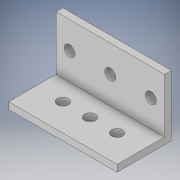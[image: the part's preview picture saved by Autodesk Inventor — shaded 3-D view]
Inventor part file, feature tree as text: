
AUTODESK INVENTOR PART (.ipt)
format: ipt  version: 2018 (Build 220112000, 112)  size: 133,120 bytes
history: native  units: in
note: dims shown in document units (in); Inventor stores cm internally (conversion verified against a paired STEP export)
features: extrude x3, sketch x3
ambient origin geometry x8: Origin, YZ Plane, XZ Plane, XY Plane, X Axis, Y Axis, Z Axis, Center Point
bodies: Solid1 (feature_tree)
feature tree (6):
  extrude  "Extrusion1"  Depth=1.0in
  extrude  "Extrusion2"  Depth=0.125in
  extrude  "Extrusion3"  Depth=2.0in
  sketch  "Sketch1"  dims[d0=0.125in d1=1.0in]
  sketch  "Sketch2"  dims[d2=1.0in d3=0.125in]
  sketch  "Sketch3"  dims[d4=2.0in d5=0.0in d6=0.5in d7=0.5in d8=0.2031in d9=0.2031in d10=0.2031in d11=2.0in d12=0.0in d13=1.0in d14=0.25in d15=0.25in d16=0.2031in d17=0.2031in d18=0.2031in d19=2.0in d20=0.0in]
